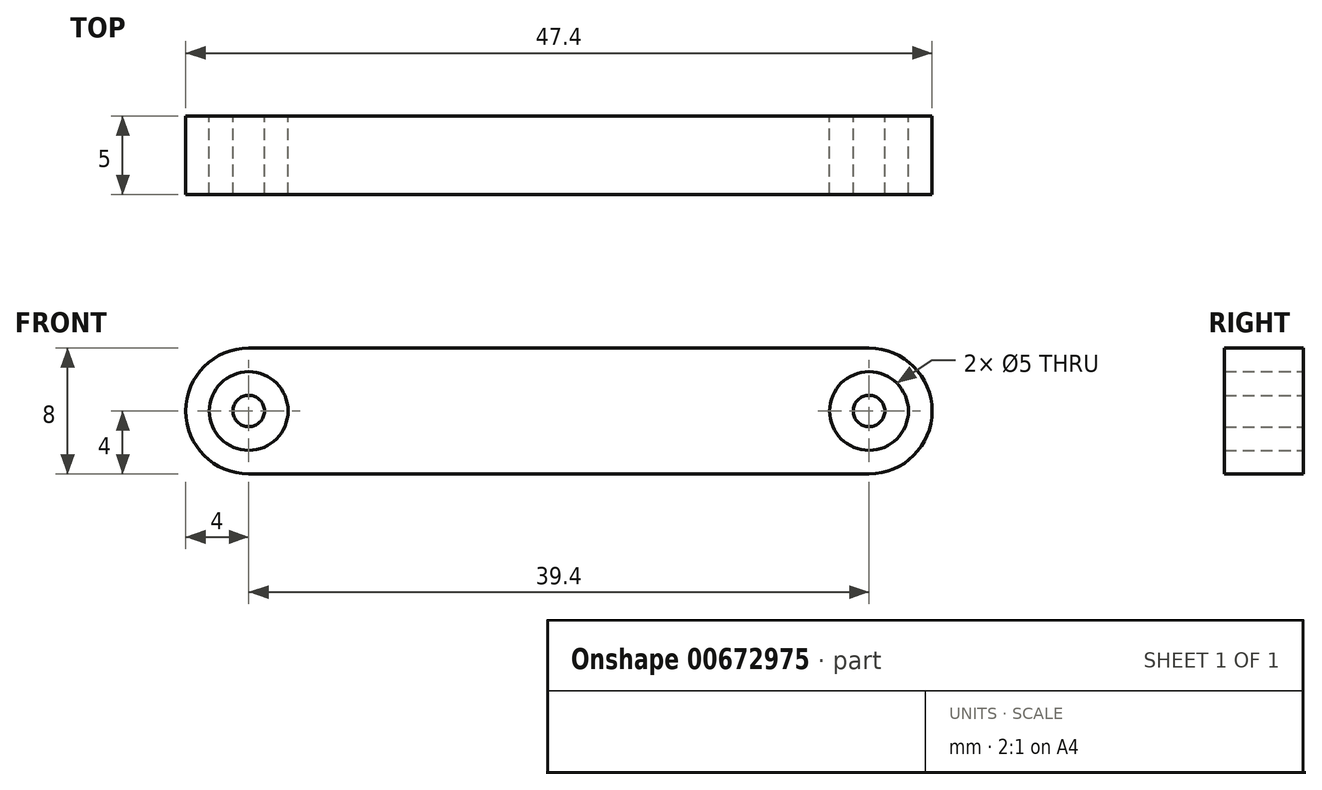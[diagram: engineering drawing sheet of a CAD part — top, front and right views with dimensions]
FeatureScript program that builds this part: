
annotation { "Feature Type Name" : "Feature", "Feature Type Description" : "" }
export const myFeature = defineFeature(function(context is Context, id is Id, definition is map)
    precondition{}
    {
        {
            var Q0;
            Q0=qCreatedBy(makeId("Front.planeOp"),FACE);
            var sketch = newSketch(context, id + "F0", { "sketchPlane" : qUnion([Q0])});
            skArc(sketch, "E0", {"start": v(0, 4) * mm, "mid": v(-4, 0) * mm, "end": v(0, -4) * mm});
            skArc(sketch, "E1", {"start": v(39.4, -4) * mm, "mid": v(43.4, 0) * mm, "end": v(39.4, 4) * mm});
            skCircle(sketch, "E2", {"center": v(39.4, 0) * mm, "radius": 2.5 * mm});
            skCircle(sketch, "E3", {"center": v(39.4, 0) * mm, "radius": 1 * mm});
            skCircle(sketch, "E4", {"center": v(0, 0) * mm, "radius": 1 * mm});
            skCircle(sketch, "E5", {"center": v(0, 0) * mm, "radius": 2.5 * mm});
            skLineSegment(sketch, "E6", {"start": v(0, 4) * mm, "end": v(39.4, 4) * mm});
            skLineSegment(sketch, "E7", {"start": v(39.4, -4) * mm, "end": v(0, -4) * mm});
            skSolve(sketch);
        }
        {
            var Q0;
            Q0 = qSketchRegion(id + "F0", true);
            var Q1;
            Q1=makeQuery(id+"F0.imprint","IMPRINT",FACE,{"disambiguationData":[TD([[makeQuery(id+"F0.imprint","IMPRINT",EDGE,{"derivedFrom":sQuery(id+"F0.wireOp",EDGE,"E4")}),1.0]])]});
            var Q2;
            Q2=makeQuery(id+"F0.imprint","IMPRINT",FACE,{"disambiguationData":[TD([[makeQuery(id+"F0.imprint","IMPRINT",EDGE,{"derivedFrom":sQuery(id+"F0.wireOp",EDGE,"E3")}),1.0]])]});
            extrude(context, id + "F1", {"entities" : qUnion([Q0, Q1, Q2]), "depth" : 5 * mm, "offsetDistance" : 25 * mm});
        }
    });
